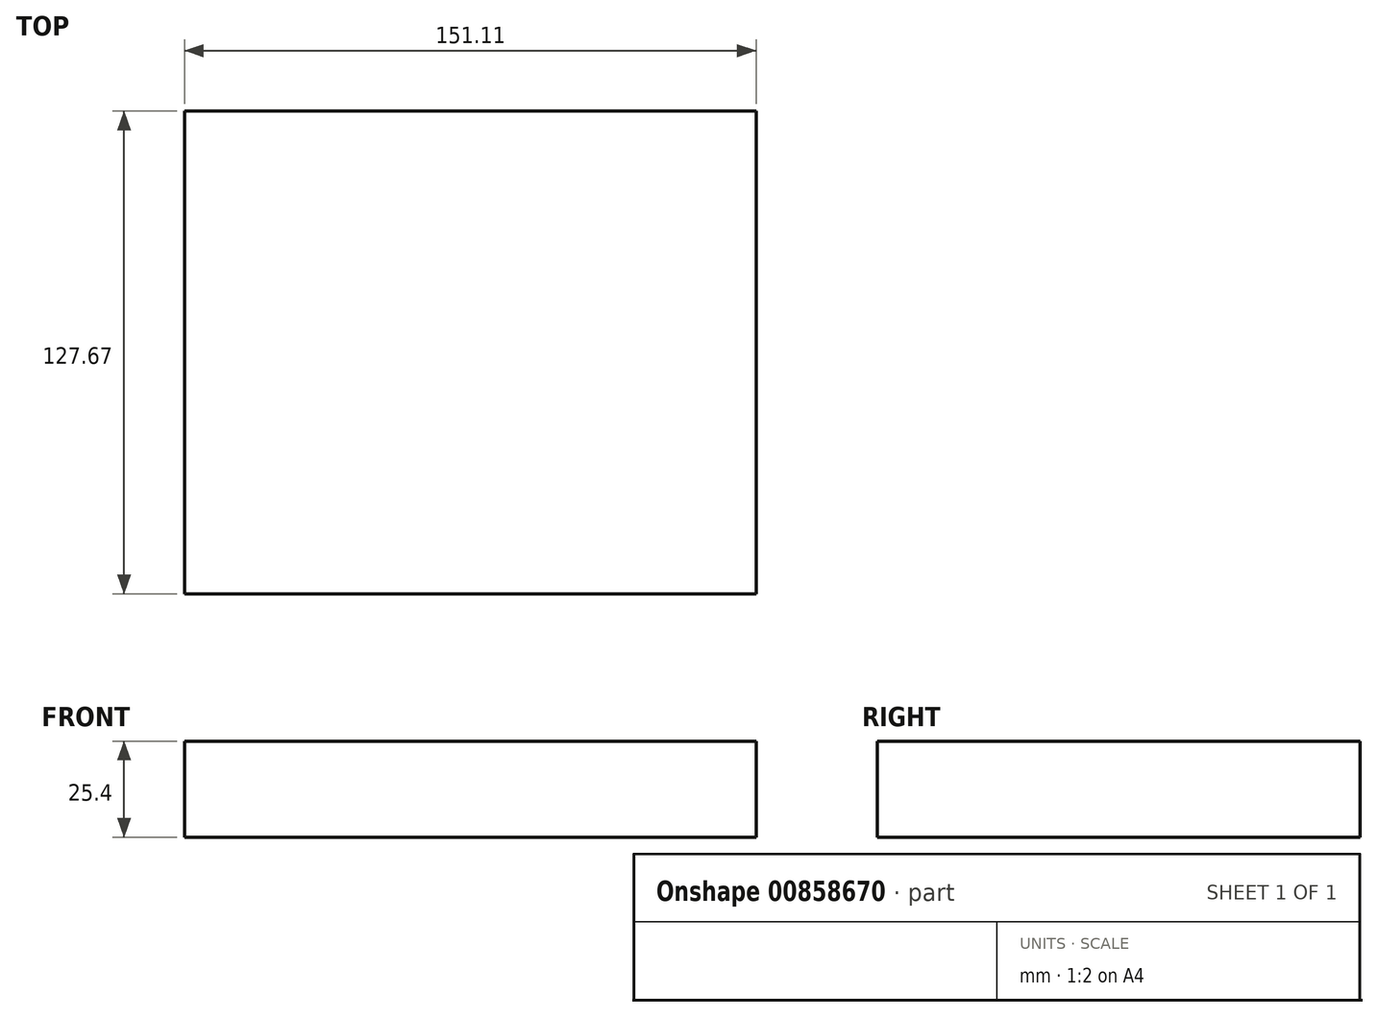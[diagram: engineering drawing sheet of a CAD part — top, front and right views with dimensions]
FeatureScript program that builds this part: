
annotation { "Feature Type Name" : "Feature", "Feature Type Description" : "" }
export const myFeature = defineFeature(function(context is Context, id is Id, definition is map)
    precondition{}
    {
        {
            var Q0;
            Q0=qCreatedBy(makeId("Top.planeOp"),FACE);
            var sketch = newSketch(context, id + "F0", { "sketchPlane" : qUnion([Q0])});
            skLineSegment(sketch, "E0.bottom", {"start": v(76.32, 75.32) * mm, "end": v(-74.8, 75.32) * mm});
            skLineSegment(sketch, "E0.top", {"start": v(76.32, -52.35) * mm, "end": v(-74.8, -52.35) * mm});
            skLineSegment(sketch, "E0.left", {"start": v(76.32, 75.32) * mm, "end": v(76.32, -52.35) * mm});
            skLineSegment(sketch, "E0.right", {"start": v(-74.8, 75.32) * mm, "end": v(-74.8, -52.35) * mm});
            skSolve(sketch);
        }
        {
            var Q0;
            Q0=makeQuery(id+"F0.imprint","IMPRINT",FACE,{"disambiguationData":[TD([[makeQuery(id+"F0.imprint","IMPRINT",EDGE,{"derivedFrom":sQuery(id+"F0.wireOp",EDGE,"E0.bottom")}),1.0]])]});
            extrude(context, id + "F1", {"entities" : qUnion([Q0]), "depth" : 25.4 * mm, "offsetDistance" : 25.4 * mm});
        }
    });
